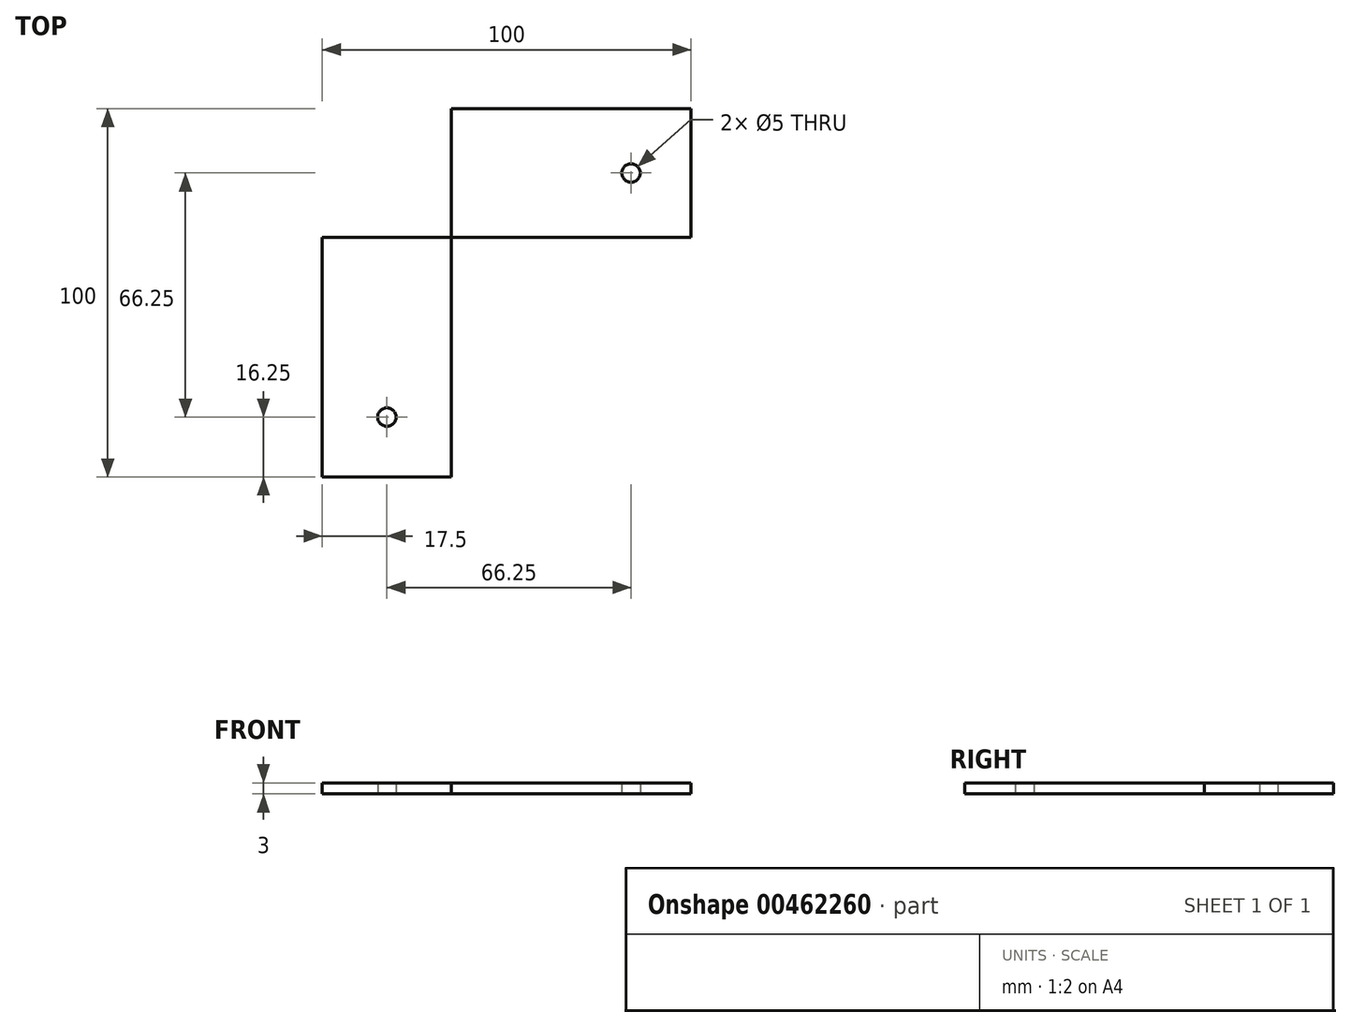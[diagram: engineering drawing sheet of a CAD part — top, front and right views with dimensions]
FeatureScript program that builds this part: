
annotation { "Feature Type Name" : "Feature", "Feature Type Description" : "" }
export const myFeature = defineFeature(function(context is Context, id is Id, definition is map)
    precondition{}
    {
        {
            var Q0;
            Q0=qCreatedBy(makeId("Top.planeOp"),FACE);
            var sketch = newSketch(context, id + "F0", { "sketchPlane" : qUnion([Q0])});
            skLineSegment(sketch, "E0.bottom", {"start": v(17.5, -50) * mm, "end": v(-17.5, -50) * mm});
            skLineSegment(sketch, "E0.top", {"start": v(17.5, 50) * mm, "end": v(-17.5, 50) * mm});
            skLineSegment(sketch, "E0.left", {"start": v(17.5, -50) * mm, "end": v(17.5, 50) * mm});
            skLineSegment(sketch, "E0.right", {"start": v(-17.5, -50) * mm, "end": v(-17.5, 50) * mm});
            skPoint(sketch, "E0.middle", {"position": v(0, 0) * mm});
            skLineSegment(sketch, "E1.bottom", {"start": v(-17.5, 50) * mm, "end": v(82.5, 50) * mm});
            skLineSegment(sketch, "E1.top", {"start": v(-17.5, 15) * mm, "end": v(82.5, 15) * mm});
            skLineSegment(sketch, "E1.left", {"start": v(-17.5, 50) * mm, "end": v(-17.5, 15) * mm});
            skLineSegment(sketch, "E1.right", {"start": v(82.5, 50) * mm, "end": v(82.5, 15) * mm});
            skCircle(sketch, "E2", {"center": v(0.3, 32.8) * mm, "radius": 2.5 * mm});
            skCircle(sketch, "E3", {"center": v(0, -33.75) * mm, "radius": 2.5 * mm});
            skCircle(sketch, "E4", {"center": v(66.25, 32.5) * mm, "radius": 2.5 * mm});
            skSolve(sketch);
        }
        {
            var Q0;
            {var subQ5=sQuery(id+"F0.wireOp",EDGE,"E1.right");Q0=makeQuery(id+"F0.imprint","IMPRINT",FACE,{"disambiguationData":[TD([[makeQuery(id+"F0.imprint","IMPRINT",EDGE,{"derivedFrom":subQ5}),-1.0]])]});}
            var Q1;
            {var subQ5=sQuery(id+"F0.wireOp",EDGE,"E1.left");Q1=makeQuery(id+"F0.imprint","IMPRINT",FACE,{"disambiguationData":[TD([[makeQuery(id+"F0.imprint","IMPRINT",EDGE,{"derivedFrom":subQ5}),1.0]])]});}
            var Q2;
            {var subQ0=sQuery(id+"F0.wireOp",EDGE,"E0.bottom");Q2=makeQuery(id+"F0.imprint","IMPRINT",FACE,{"disambiguationData":[TD([[makeQuery(id+"F0.imprint","IMPRINT",EDGE,{"derivedFrom":subQ0}),-1.0]])]});}
            extrude(context, id + "F1", {"entities" : qUnion([Q0, Q1, Q2]), "depth" : 3 * mm});
        }
    });
